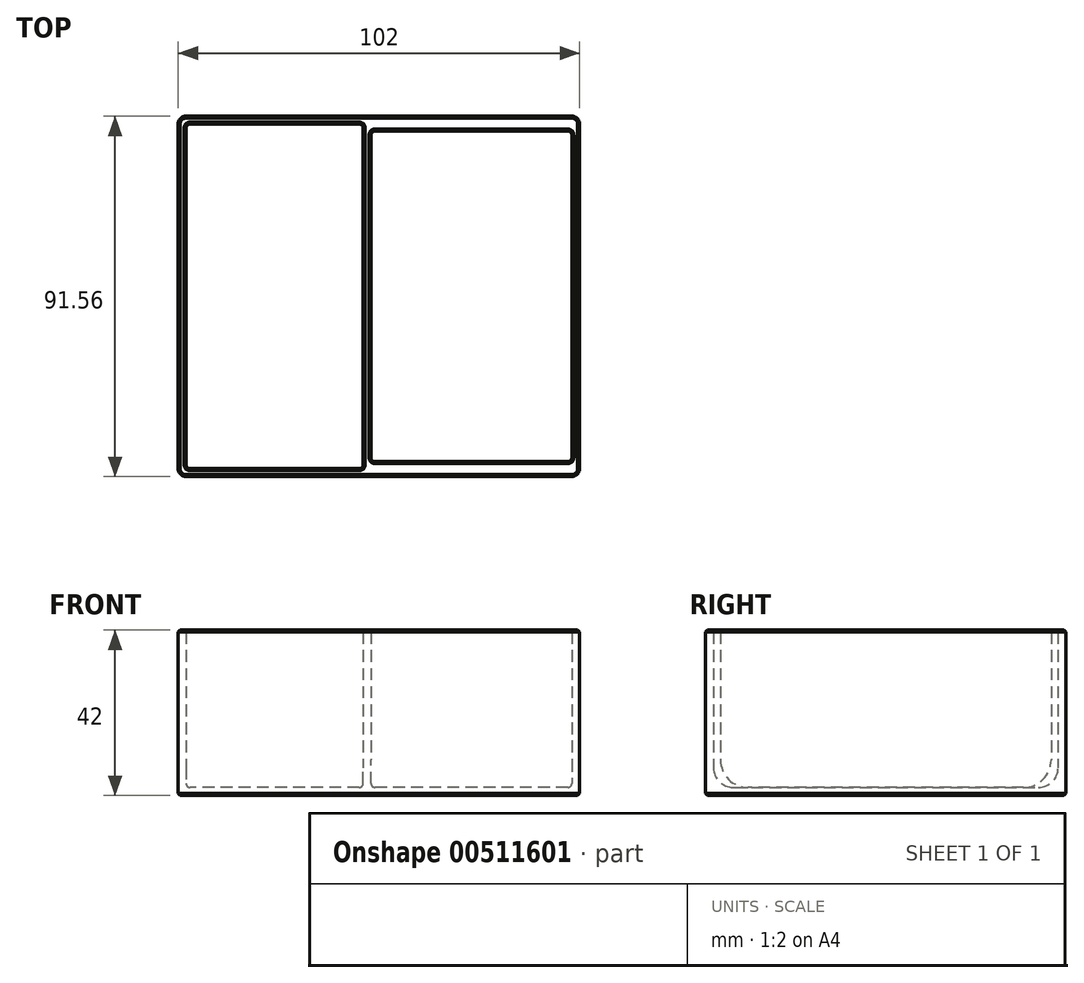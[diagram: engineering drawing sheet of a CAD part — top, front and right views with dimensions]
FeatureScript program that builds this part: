
annotation { "Feature Type Name" : "Feature", "Feature Type Description" : "" }
export const myFeature = defineFeature(function(context is Context, id is Id, definition is map)
    precondition{}
    {
        {
            var Q0;
            Q0=qCreatedBy(makeId("Top.planeOp"),FACE);
            var sketch = newSketch(context, id + "F0", { "sketchPlane" : qUnion([Q0])});
            skLineSegment(sketch, "E0.bottom", {"start": v(-46, 43.77) * mm, "end": v(-1, 43.77) * mm});
            skLineSegment(sketch, "E0.top", {"start": v(-46, -43.78) * mm, "end": v(-1, -43.78) * mm});
            skLineSegment(sketch, "E0.left", {"start": v(-46, 43.78) * mm, "end": v(-46, -43.78) * mm});
            skLineSegment(sketch, "E0.right", {"start": v(-1, 43.78) * mm, "end": v(-1, -43.78) * mm});
            skLineSegment(sketch, "E1.bottom", {"start": v(1, -42) * mm, "end": v(52, -42) * mm});
            skLineSegment(sketch, "E1.top", {"start": v(1, 42) * mm, "end": v(52, 42) * mm});
            skLineSegment(sketch, "E1.left", {"start": v(1, -42) * mm, "end": v(1, 42) * mm});
            skLineSegment(sketch, "E1.right", {"start": v(52, -42) * mm, "end": v(52, 42) * mm});
            skLineSegment(sketch, "E2.bottom", {"start": v(-48, -45.78) * mm, "end": v(54, -45.78) * mm});
            skLineSegment(sketch, "E2.top", {"start": v(-48, 45.77) * mm, "end": v(54, 45.77) * mm});
            skLineSegment(sketch, "E2.left", {"start": v(-48, -45.78) * mm, "end": v(-48, 45.77) * mm});
            skLineSegment(sketch, "E2.right", {"start": v(54, -45.77) * mm, "end": v(54, 45.78) * mm});
            skSolve(sketch);
        }
        {
            var Q0;
            Q0=makeQuery(id+"F0.imprint","IMPRINT",FACE,{"disambiguationData":[TD([[makeQuery(id+"F0.imprint","IMPRINT",EDGE,{"derivedFrom":sQuery(id+"F0.wireOp",EDGE,"E0.bottom")}),1.0]])]});
            var Q1;
            Q1=makeQuery(id+"F0.imprint","IMPRINT",FACE,{"disambiguationData":[TD([[makeQuery(id+"F0.imprint","IMPRINT",EDGE,{"derivedFrom":sQuery(id+"F0.wireOp",EDGE,"E0.bottom")}),-1.0]])]});
            var Q2;
            Q2=makeQuery(id+"F0.imprint","IMPRINT",FACE,{"disambiguationData":[TD([[makeQuery(id+"F0.imprint","IMPRINT",EDGE,{"derivedFrom":sQuery(id+"F0.wireOp",EDGE,"E1.bottom")}),1.0]])]});
            extrude(context, id + "F1", {"entities" : qUnion([Q0, Q1, Q2]), "depth" : 2 * mm, "offsetDistance" : 25 * mm});
        }
        {
            var Q0;
            Q0=makeQuery(id+"F0.imprint","IMPRINT",FACE,{"disambiguationData":[TD([[makeQuery(id+"F0.imprint","IMPRINT",EDGE,{"derivedFrom":sQuery(id+"F0.wireOp",EDGE,"E0.bottom")}),1.0]])]});
            extrude(context, id + "F2", {"entities" : qUnion([Q0]), "operationType" : NewBodyOperationType.ADD, "depth" : 42 * mm, "offsetDistance" : 25 * mm});
        }
        {
            var Q0;
            Q0=makeQuery(id+"F2.boolean.opBoolean","INTERSECT",EDGE,{"derivedFrom":[makeQuery(id+"F1.opExtrude","CAP_FACE",FACE,{"disambiguationData":[OSD([sQuery(id+"F0.wireOp",EDGE,"E2.bottom"),sQuery(id+"F0.wireOp",EDGE,"E2.top"),sQuery(id+"F0.wireOp",EDGE,"E2.left"),sQuery(id+"F0.wireOp",EDGE,"E2.right")])],"isStart":false}),makeQuery(id+"F2.opExtrude","SWEPT_FACE",FACE,{"disambiguationData":[OSD([sQuery(id+"F0.wireOp",EDGE,"E1.top")])]})]});
            var Q1;
            Q1=makeQuery(id+"F2.boolean.opBoolean","INTERSECT",EDGE,{"derivedFrom":[makeQuery(id+"F1.opExtrude","CAP_FACE",FACE,{"disambiguationData":[OSD([sQuery(id+"F0.wireOp",EDGE,"E2.bottom"),sQuery(id+"F0.wireOp",EDGE,"E2.top"),sQuery(id+"F0.wireOp",EDGE,"E2.left"),sQuery(id+"F0.wireOp",EDGE,"E2.right")])],"isStart":false}),makeQuery(id+"F2.opExtrude","SWEPT_FACE",FACE,{"disambiguationData":[OSD([sQuery(id+"F0.wireOp",EDGE,"E1.bottom")])]})]});
            fillet(context, id + "F3", {"entities" : qUnion([Q0, Q1]), "tangentPropagation" : true, "radius" : 7 * mm, "defaultsChanged" : true, "vertexSettings" : [], "allowEdgeOverflow" : false});
        }
        {
            var Q0;
            Q0=makeQuery(id+"F2.boolean.opBoolean","INTERSECT",EDGE,{"derivedFrom":[makeQuery(id+"F1.opExtrude","CAP_FACE",FACE,{"disambiguationData":[OSD([sQuery(id+"F0.wireOp",EDGE,"E2.bottom"),sQuery(id+"F0.wireOp",EDGE,"E2.top"),sQuery(id+"F0.wireOp",EDGE,"E2.left"),sQuery(id+"F0.wireOp",EDGE,"E2.right")])],"isStart":false}),makeQuery(id+"F2.opExtrude","SWEPT_FACE",FACE,{"disambiguationData":[OSD([sQuery(id+"F0.wireOp",EDGE,"E0.bottom")])]})]});
            var Q1;
            Q1=makeQuery(id+"F2.boolean.opBoolean","INTERSECT",EDGE,{"derivedFrom":[makeQuery(id+"F1.opExtrude","CAP_FACE",FACE,{"disambiguationData":[OSD([sQuery(id+"F0.wireOp",EDGE,"E2.bottom"),sQuery(id+"F0.wireOp",EDGE,"E2.top"),sQuery(id+"F0.wireOp",EDGE,"E2.left"),sQuery(id+"F0.wireOp",EDGE,"E2.right")])],"isStart":false}),makeQuery(id+"F2.opExtrude","SWEPT_FACE",FACE,{"disambiguationData":[OSD([sQuery(id+"F0.wireOp",EDGE,"E0.top")])]})]});
            fillet(context, id + "F4", {"entities" : qUnion([Q0, Q1]), "tangentPropagation" : true, "radius" : 5 * mm, "defaultsChanged" : false, "vertexSettings" : [], "allowEdgeOverflow" : false});
        }
        {
            var Q0;
            {var subQ0=sQuery(id+"F0.wireOp",EDGE,"E2.right");var subQ1=sQuery(id+"F0.wireOp",EDGE,"E2.bottom");Q0=makeQuery(id+"F2.boolean.opBoolean","MERGE",EDGE,{"derivedFrom":[makeQuery(id+"F1.opExtrude","SWEPT_EDGE",EDGE,{"disambiguationData":[OSD([subQ1,subQ0])]}),makeQuery(id+"F2.opExtrude","SWEPT_EDGE",EDGE,{"disambiguationData":[OSD([subQ1,subQ0])]})]});}
            var Q1;
            {var subQ0=sQuery(id+"F0.wireOp",EDGE,"E2.right");var subQ1=sQuery(id+"F0.wireOp",EDGE,"E2.top");Q1=makeQuery(id+"F2.boolean.opBoolean","MERGE",EDGE,{"derivedFrom":[makeQuery(id+"F1.opExtrude","SWEPT_EDGE",EDGE,{"disambiguationData":[OSD([subQ1,subQ0])]}),makeQuery(id+"F2.opExtrude","SWEPT_EDGE",EDGE,{"disambiguationData":[OSD([subQ1,subQ0])]})]});}
            var Q2;
            {var subQ0=sQuery(id+"F0.wireOp",EDGE,"E2.left");var subQ1=sQuery(id+"F0.wireOp",EDGE,"E2.top");Q2=makeQuery(id+"F2.boolean.opBoolean","MERGE",EDGE,{"derivedFrom":[makeQuery(id+"F1.opExtrude","SWEPT_EDGE",EDGE,{"disambiguationData":[OSD([subQ1,subQ0])]}),makeQuery(id+"F2.opExtrude","SWEPT_EDGE",EDGE,{"disambiguationData":[OSD([subQ1,subQ0])]})]});}
            var Q3;
            {var subQ0=sQuery(id+"F0.wireOp",EDGE,"E2.left");var subQ1=sQuery(id+"F0.wireOp",EDGE,"E2.bottom");Q3=makeQuery(id+"F2.boolean.opBoolean","MERGE",EDGE,{"derivedFrom":[makeQuery(id+"F1.opExtrude","SWEPT_EDGE",EDGE,{"disambiguationData":[OSD([subQ1,subQ0])]}),makeQuery(id+"F2.opExtrude","SWEPT_EDGE",EDGE,{"disambiguationData":[OSD([subQ1,subQ0])]})]});}
            fillet(context, id + "F5", {"entities" : qUnion([Q0, Q1, Q2, Q3]), "tangentPropagation" : true, "radius" : 2 * mm, "defaultsChanged" : false, "vertexSettings" : [], "allowEdgeOverflow" : false});
        }
        {
            var Q0;
            Q0=makeQuery(id+"F1.opExtrude","CAP_FACE",FACE,{"disambiguationData":[OSD([sQuery(id+"F0.wireOp",EDGE,"E2.bottom"),sQuery(id+"F0.wireOp",EDGE,"E2.top"),sQuery(id+"F0.wireOp",EDGE,"E2.left"),sQuery(id+"F0.wireOp",EDGE,"E2.right")])],"isStart":true});
            chamfer(context, id + "F6", {"entities" : qUnion([Q0]), "width" : 0.5 * mm, "tangentPropagation" : true});
        }
        {
            var Q0;
            Q0=makeQuery(id+"F2.opExtrude","SWEPT_EDGE",EDGE,{"disambiguationData":[OSD([sQuery(id+"F0.wireOp",EDGE,"E0.bottom"),sQuery(id+"F0.wireOp",EDGE,"E0.left")])]});
            var Q1;
            Q1=makeQuery(id+"F2.boolean.opBoolean","INTERSECT",EDGE,{"derivedFrom":[makeQuery(id+"F1.opExtrude","CAP_FACE",FACE,{"disambiguationData":[OSD([sQuery(id+"F0.wireOp",EDGE,"E2.bottom"),sQuery(id+"F0.wireOp",EDGE,"E2.top"),sQuery(id+"F0.wireOp",EDGE,"E2.left"),sQuery(id+"F0.wireOp",EDGE,"E2.right")])],"isStart":false}),makeQuery(id+"F2.opExtrude","SWEPT_FACE",FACE,{"disambiguationData":[OSD([sQuery(id+"F0.wireOp",EDGE,"E0.right")])]})]});
            var Q2;
            Q2=makeQuery(id+"F2.opExtrude","SWEPT_EDGE",EDGE,{"disambiguationData":[OSD([sQuery(id+"F0.wireOp",EDGE,"E1.bottom"),sQuery(id+"F0.wireOp",EDGE,"E1.left")])]});
            var Q3;
            Q3=makeQuery(id+"F2.opExtrude","SWEPT_EDGE",EDGE,{"disambiguationData":[OSD([sQuery(id+"F0.wireOp",EDGE,"E1.top"),sQuery(id+"F0.wireOp",EDGE,"E1.right")])]});
            fillet(context, id + "F7", {"entities" : qUnion([Q0, Q1, Q2, Q3]), "tangentPropagation" : true, "radius" : 1 * mm, "defaultsChanged" : true, "vertexSettings" : [], "allowEdgeOverflow" : false});
        }
        {
            var Q0;
            Q0=makeQuery(id+"F2.opExtrude","CAP_FACE",FACE,{"disambiguationData":[OSD([sQuery(id+"F0.wireOp",EDGE,"E0.bottom"),sQuery(id+"F0.wireOp",EDGE,"E0.top"),sQuery(id+"F0.wireOp",EDGE,"E0.left"),sQuery(id+"F0.wireOp",EDGE,"E0.right"),sQuery(id+"F0.wireOp",EDGE,"E1.bottom"),sQuery(id+"F0.wireOp",EDGE,"E1.top"),sQuery(id+"F0.wireOp",EDGE,"E1.left"),sQuery(id+"F0.wireOp",EDGE,"E1.right"),sQuery(id+"F0.wireOp",EDGE,"E2.bottom"),sQuery(id+"F0.wireOp",EDGE,"E2.top"),sQuery(id+"F0.wireOp",EDGE,"E2.left"),sQuery(id+"F0.wireOp",EDGE,"E2.right")])],"isStart":false});
            chamfer(context, id + "F8", {"entities" : qUnion([Q0]), "width" : 0.5 * mm, "tangentPropagation" : true});
        }
    });
